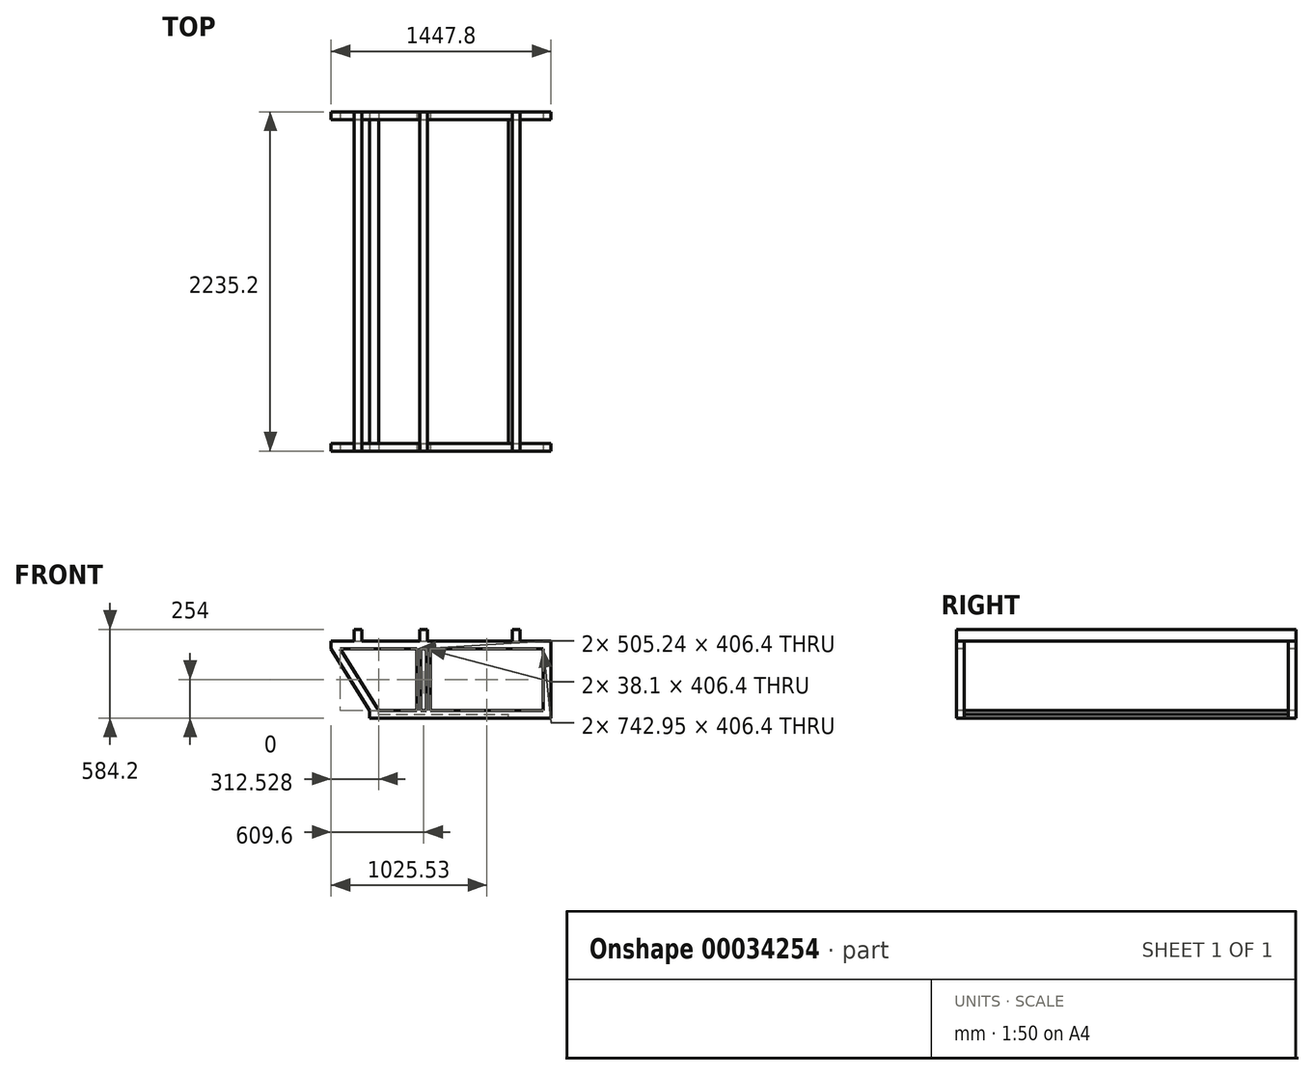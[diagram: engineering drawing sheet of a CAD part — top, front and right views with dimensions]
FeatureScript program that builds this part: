
annotation { "Feature Type Name" : "Feature", "Feature Type Description" : "" }
export const myFeature = defineFeature(function(context is Context, id is Id, definition is map)
    precondition{}
    {
        {
            var Q0;
            Q0=qCreatedBy(makeId("Front.planeOp"),FACE);
            var sketch = newSketch(context, id + "F0", { "sketchPlane" : qUnion([Q0])});
            skLineSegment(sketch, "E0.bottom", {"start": v(0, 0) * mm, "end": v(-1447.8, 0) * mm});
            skLineSegment(sketch, "E0.top", {"start": v(0, -584.2) * mm, "end": v(-1447.8, -584.2) * mm});
            skLineSegment(sketch, "E0.left", {"start": v(0, 0) * mm, "end": v(0, -584.2) * mm});
            skLineSegment(sketch, "E0.right", {"start": v(-1447.8, 0) * mm, "end": v(-1447.8, -584.2) * mm});
            skSolve(sketch);
        }
        {
            var Q0;
            Q0=makeQuery(id+"F0.imprint","IMPRINT",FACE,{"disambiguationData":[TD([[makeQuery(id+"F0.imprint","IMPRINT",EDGE,{"derivedFrom":sQuery(id+"F0.wireOp",EDGE,"E0.bottom")}),1.0]])]});
            extrude(context, id + "F1", {"entities" : qUnion([Q0]), "depth" : 2235.2 * mm});
        }
        {
            var Q0;
            Q0=makeQuery(id+"F1.opExtrude","CAP_FACE",FACE,{"disambiguationData":[OSD([sQuery(id+"F0.wireOp",EDGE,"E0.bottom"),sQuery(id+"F0.wireOp",EDGE,"E0.top"),sQuery(id+"F0.wireOp",EDGE,"E0.left"),sQuery(id+"F0.wireOp",EDGE,"E0.right")])],"isStart":false});
            var sketch = newSketch(context, id + "F2", { "sketchPlane" : qUnion([Q0])});
            skLineSegment(sketch, "E1.bottom", {"start": v(-1447.8, 0) * mm, "end": v(-1295.4, 0) * mm});
            skLineSegment(sketch, "E1.top", {"start": v(-1447.8, -76.2) * mm, "end": v(-1295.4, -76.2) * mm});
            skLineSegment(sketch, "E1.left", {"start": v(-1447.8, 0) * mm, "end": v(-1447.8, -76.2) * mm});
            skLineSegment(sketch, "E1.right", {"start": v(-1295.4, 0) * mm, "end": v(-1295.4, -76.2) * mm});
            skLineSegment(sketch, "E2.bottom", {"start": v(-1244.6, 0) * mm, "end": v(-863.6, 0) * mm});
            skLineSegment(sketch, "E2.top", {"start": v(-1244.6, -76.2) * mm, "end": v(-863.6, -76.2) * mm});
            skLineSegment(sketch, "E2.left", {"start": v(-1244.6, 0) * mm, "end": v(-1244.6, -76.2) * mm});
            skLineSegment(sketch, "E2.right", {"start": v(-863.6, 0) * mm, "end": v(-863.6, -76.2) * mm});
            skLineSegment(sketch, "E3.bottom", {"start": v(-812.8, 0) * mm, "end": v(-254, 0) * mm});
            skLineSegment(sketch, "E3.top", {"start": v(-812.8, -76.2) * mm, "end": v(-254, -76.2) * mm});
            skLineSegment(sketch, "E3.left", {"start": v(-812.8, 0) * mm, "end": v(-812.8, -76.2) * mm});
            skLineSegment(sketch, "E3.right", {"start": v(-254, 0) * mm, "end": v(-254, -76.2) * mm});
            skLineSegment(sketch, "E4.bottom", {"start": v(-203.2, 0) * mm, "end": v(0, 0) * mm});
            skLineSegment(sketch, "E4.top", {"start": v(-203.2, -76.2) * mm, "end": v(0, -76.2) * mm});
            skLineSegment(sketch, "E4.left", {"start": v(-203.2, 0) * mm, "end": v(-203.2, -76.2) * mm});
            skLineSegment(sketch, "E4.right", {"start": v(0, 0) * mm, "end": v(0, -76.2) * mm});
            skSolve(sketch);
        }
        {
            var Q0;
            Q0=makeQuery(id+"F2.imprint","IMPRINT",FACE,{"disambiguationData":[TD([[makeQuery(id+"F2.imprint","IMPRINT",EDGE,{"derivedFrom":sQuery(id+"F2.wireOp",EDGE,"E1.bottom")}),1.0]])]});
            var Q1;
            Q1=makeQuery(id+"F2.imprint","IMPRINT",FACE,{"disambiguationData":[TD([[makeQuery(id+"F2.imprint","IMPRINT",EDGE,{"derivedFrom":sQuery(id+"F2.wireOp",EDGE,"E2.bottom")}),1.0]])]});
            var Q2;
            Q2=makeQuery(id+"F2.imprint","IMPRINT",FACE,{"disambiguationData":[TD([[makeQuery(id+"F2.imprint","IMPRINT",EDGE,{"derivedFrom":sQuery(id+"F2.wireOp",EDGE,"E3.bottom")}),1.0]])]});
            var Q3;
            Q3=makeQuery(id+"F2.imprint","IMPRINT",FACE,{"disambiguationData":[TD([[makeQuery(id+"F2.imprint","IMPRINT",EDGE,{"derivedFrom":sQuery(id+"F2.wireOp",EDGE,"E4.bottom")}),1.0]])]});
            extrude(context, id + "F3", {"entities" : qUnion([Q0, Q1, Q2, Q3]), "operationType" : NewBodyOperationType.REMOVE, "endBound" : BoundingType.THROUGH_ALL, "oppositeDirection" : true, "depth" : 25.4 * mm});
        }
        {
            var Q0;
            Q0=makeQuery(id+"F1.opExtrude","CAP_FACE",FACE,{"disambiguationData":[OSD([sQuery(id+"F0.wireOp",EDGE,"E0.bottom"),sQuery(id+"F0.wireOp",EDGE,"E0.top"),sQuery(id+"F0.wireOp",EDGE,"E0.left"),sQuery(id+"F0.wireOp",EDGE,"E0.right")])],"isStart":false});
            var sketch = newSketch(context, id + "F4", { "sketchPlane" : qUnion([Q0])});
            skLineSegment(sketch, "E5.right", {"start": v(-1193.8, -584.2) * mm, "end": v(-1193.8, -533.4) * mm});
            skLineSegment(sketch, "E6", {"start": v(-1447.8, -127) * mm, "end": v(-1193.8, -533.4) * mm});
            skLineSegment(sketch, "E7", {"start": v(-1447.8, -127) * mm, "end": v(-1447.8, -584.2) * mm});
            skLineSegment(sketch, "E8", {"start": v(-1447.8, -584.2) * mm, "end": v(-1193.8, -584.2) * mm});
            skLineSegment(sketch, "E9.top", {"start": v(-1387.9, -127) * mm, "end": v(-819.15, -127) * mm});
            skLineSegment(sketch, "E10", {"start": v(-1387.9, -127) * mm, "end": v(-1133.9, -533.4) * mm});
            skPoint(sketch, "E11.startSnap0", {"position": v(-838.2, 0) * mm});
            skLineSegment(sketch, "E12.bottom", {"start": v(-857.25, -127) * mm, "end": v(-882.65, -127) * mm});
            skLineSegment(sketch, "E12.top", {"start": v(-857.25, -533.4) * mm, "end": v(-882.65, -533.4) * mm});
            skLineSegment(sketch, "E12.left", {"start": v(-857.25, -127) * mm, "end": v(-857.25, -533.4) * mm});
            skLineSegment(sketch, "E12.right", {"start": v(-882.65, -127) * mm, "end": v(-882.65, -533.4) * mm});
            skLineSegment(sketch, "E13.left", {"start": v(-819.15, -127) * mm, "end": v(-819.15, -533.4) * mm});
            skPoint(sketch, "E11.start.orphan", {"position": v(-838.2, -127) * mm});
            skLineSegment(sketch, "E14.trimOffspring", {"start": v(-819.15, -533.4) * mm, "end": v(-1133.9, -533.4) * mm});
            skPoint(sketch, "E9.right.end.orphan", {"position": v(0, -127) * mm});
            skSolve(sketch);
        }
        {
            var Q0;
            Q0=makeQuery(id+"F4.imprint","IMPRINT",FACE,{"disambiguationData":[TD([[makeQuery(id+"F4.imprint","IMPRINT",EDGE,{"derivedFrom":sQuery(id+"F4.wireOp",EDGE,"E5.right")}),1.0]])]});
            var Q1;
            {var subQ1=sQuery(id+"F4.wireOp",EDGE,"E10");Q1=makeQuery(id+"F4.imprint","IMPRINT",FACE,{"disambiguationData":[TD([[makeQuery(id+"F4.imprint","IMPRINT",EDGE,{"derivedFrom":subQ1}),1.0]])]});}
            var Q2;
            {var subQ1=sQuery(id+"F4.wireOp",EDGE,"E12.left");Q2=makeQuery(id+"F4.imprint","IMPRINT",FACE,{"disambiguationData":[TD([[makeQuery(id+"F4.imprint","IMPRINT",EDGE,{"derivedFrom":subQ1}),1.0]])]});}
            extrude(context, id + "F5", {"entities" : qUnion([Q0, Q1, Q2]), "operationType" : NewBodyOperationType.REMOVE, "endBound" : BoundingType.THROUGH_ALL, "oppositeDirection" : true, "depth" : 25.4 * mm});
        }
        {
            var Q0;
            Q0=makeQuery(id+"F1.opExtrude","CAP_FACE",FACE,{"disambiguationData":[OSD([sQuery(id+"F0.wireOp",EDGE,"E0.bottom"),sQuery(id+"F0.wireOp",EDGE,"E0.top"),sQuery(id+"F0.wireOp",EDGE,"E0.left"),sQuery(id+"F0.wireOp",EDGE,"E0.right")])],"isStart":false});
            var sketch = newSketch(context, id + "F6", { "sketchPlane" : qUnion([Q0])});
            skLineSegment(sketch, "E15.bottom", {"start": v(-793.75, -127) * mm, "end": v(-50.8, -127) * mm});
            skLineSegment(sketch, "E15.top", {"start": v(-793.75, -533.4) * mm, "end": v(-50.8, -533.4) * mm});
            skLineSegment(sketch, "E15.left", {"start": v(-793.75, -127) * mm, "end": v(-793.75, -533.4) * mm});
            skLineSegment(sketch, "E15.right", {"start": v(-50.8, -127) * mm, "end": v(-50.8, -533.4) * mm});
            skSolve(sketch);
        }
        {
            var Q0;
            Q0=makeQuery(id+"F6.imprint","IMPRINT",FACE,{"disambiguationData":[TD([[makeQuery(id+"F6.imprint","IMPRINT",EDGE,{"derivedFrom":sQuery(id+"F6.wireOp",EDGE,"E15.bottom")}),-1.0]])]});
            extrude(context, id + "F7", {"entities" : qUnion([Q0]), "operationType" : NewBodyOperationType.REMOVE, "endBound" : BoundingType.THROUGH_ALL, "oppositeDirection" : true, "depth" : 25.4 * mm});
        }
        {
            var Q0;
            Q0=makeQuery(id+"F1.opExtrude","SWEPT_FACE",FACE,{"disambiguationData":[OSD([sQuery(id+"F0.wireOp",EDGE,"E0.left")])]});
            var sketch = newSketch(context, id + "F8", { "sketchPlane" : qUnion([Q0])});
            skLineSegment(sketch, "E16.bottom", {"start": v(-2184.4, -76.2) * mm, "end": v(-50.8, -76.2) * mm});
            skLineSegment(sketch, "E16.top", {"start": v(-2184.4, -533.4) * mm, "end": v(-50.8, -533.4) * mm});
            skLineSegment(sketch, "E16.left", {"start": v(-2184.4, -76.2) * mm, "end": v(-2184.4, -533.4) * mm});
            skLineSegment(sketch, "E16.right", {"start": v(-50.8, -76.2) * mm, "end": v(-50.8, -533.4) * mm});
            skSolve(sketch);
        }
        {
            var Q0;
            Q0=makeQuery(id+"F8.imprint","IMPRINT",FACE,{"disambiguationData":[TD([[makeQuery(id+"F8.imprint","IMPRINT",EDGE,{"derivedFrom":sQuery(id+"F8.wireOp",EDGE,"E16.bottom")}),-1.0]])]});
            var Q1;
            Q1=makeQuery(id+"F8.imprint","IMPRINT",FACE,{"disambiguationData":[TD([[makeQuery(id+"F8.imprint","IMPRINT",EDGE,{"derivedFrom":sQuery(id+"F8.wireOp",EDGE,"E16.bottom")}),1.0]])]});
            extrude(context, id + "F9", {"entities" : qUnion([Q0, Q1]), "operationType" : NewBodyOperationType.REMOVE, "endBound" : BoundingType.THROUGH_ALL, "oppositeDirection" : true, "depth" : 25.4 * mm});
        }
        {
            var Q0;
            Q0=qCreatedBy(makeId("Top.planeOp"),FACE);
            var sketch = newSketch(context, id + "F10", { "sketchPlane" : qUnion([Q0])});
            skLineSegment(sketch, "E17.bottom", {"start": v(-1244.6, -50.8) * mm, "end": v(-863.6, -50.8) * mm});
            skLineSegment(sketch, "E17.top", {"start": v(-1244.6, -2184.4) * mm, "end": v(-863.6, -2184.4) * mm});
            skLineSegment(sketch, "E17.left", {"start": v(-1244.6, -50.8) * mm, "end": v(-1244.6, -2184.4) * mm});
            skLineSegment(sketch, "E17.right", {"start": v(-863.6, -50.8) * mm, "end": v(-863.6, -2184.4) * mm});
            skLineSegment(sketch, "E18.bottom", {"start": v(-812.8, -50.8) * mm, "end": v(-254, -50.8) * mm});
            skLineSegment(sketch, "E18.top", {"start": v(-812.8, -2184.4) * mm, "end": v(-254, -2184.4) * mm});
            skLineSegment(sketch, "E18.left", {"start": v(-812.8, -50.8) * mm, "end": v(-812.8, -2184.4) * mm});
            skLineSegment(sketch, "E18.right", {"start": v(-254, -50.8) * mm, "end": v(-254, -2184.4) * mm});
            skLineSegment(sketch, "E19.bottom", {"start": v(0, -50.8) * mm, "end": v(-203.2, -50.8) * mm});
            skLineSegment(sketch, "E19.top", {"start": v(0, -2184.4) * mm, "end": v(-203.2, -2184.4) * mm});
            skLineSegment(sketch, "E19.left", {"start": v(0, -50.8) * mm, "end": v(0, -2184.4) * mm});
            skLineSegment(sketch, "E19.right", {"start": v(-203.2, -50.8) * mm, "end": v(-203.2, -2184.4) * mm});
            skLineSegment(sketch, "E20.bottom", {"start": v(-1447.8, -50.8) * mm, "end": v(-1295.4, -50.8) * mm});
            skLineSegment(sketch, "E20.top", {"start": v(-1447.8, -2184.4) * mm, "end": v(-1295.4, -2184.4) * mm});
            skLineSegment(sketch, "E20.left", {"start": v(-1447.8, -50.8) * mm, "end": v(-1447.8, -2184.4) * mm});
            skLineSegment(sketch, "E20.right", {"start": v(-1295.4, -50.8) * mm, "end": v(-1295.4, -2184.4) * mm});
            skSolve(sketch);
        }
        {
            var Q0;
            Q0=makeQuery(id+"F10.imprint","IMPRINT",FACE,{"disambiguationData":[TD([[makeQuery(id+"F10.imprint","IMPRINT",EDGE,{"derivedFrom":sQuery(id+"F10.wireOp",EDGE,"E20.bottom")}),-1.0]])]});
            var Q1;
            Q1=makeQuery(id+"F10.imprint","IMPRINT",FACE,{"disambiguationData":[TD([[makeQuery(id+"F10.imprint","IMPRINT",EDGE,{"derivedFrom":sQuery(id+"F10.wireOp",EDGE,"E17.bottom")}),-1.0]])]});
            var Q2;
            Q2=makeQuery(id+"F10.imprint","IMPRINT",FACE,{"disambiguationData":[TD([[makeQuery(id+"F10.imprint","IMPRINT",EDGE,{"derivedFrom":sQuery(id+"F10.wireOp",EDGE,"E18.bottom")}),-1.0]])]});
            var Q3;
            Q3=makeQuery(id+"F10.imprint","IMPRINT",FACE,{"disambiguationData":[TD([[makeQuery(id+"F10.imprint","IMPRINT",EDGE,{"derivedFrom":sQuery(id+"F10.wireOp",EDGE,"E19.bottom")}),1.0]])]});
            extrude(context, id + "F11", {"entities" : qUnion([Q0, Q1, Q2, Q3]), "operationType" : NewBodyOperationType.REMOVE, "oppositeDirection" : true, "depth" : 127 * mm});
        }
        {
            var Q0;
            {var subQ0=sQuery(id+"F4.wireOp",EDGE,"E14.trimOffspring");Q0=makeQuery(id+"F9.boolean.opBoolean","MERGE",FACE,{"derivedFrom":[makeQuery(id+"F5.boolean.opBoolean","COPY",FACE,{"derivedFrom":makeQuery(id+"F5.opExtrude","SWEPT_FACE",FACE,{"disambiguationData":[OSD([subQ0]),TDD([makeQuery(id+"F4.imprint","IMPRINT",EDGE,{"disambiguationData":[TD([[makeQuery(id+"F4.imprint","INTERSECT",VERTEX,{"derivedFrom":[sQuery(id+"F4.wireOp",EDGE,"E12.left"),subQ0]}),1.0]])],"derivedFrom":subQ0})])]})}),makeQuery(id+"F5.boolean.opBoolean","COPY",FACE,{"derivedFrom":makeQuery(id+"F5.opExtrude","SWEPT_FACE",FACE,{"disambiguationData":[OSD([subQ0]),TDD([makeQuery(id+"F4.imprint","IMPRINT",EDGE,{"disambiguationData":[TD([[makeQuery(id+"F4.imprint","INTERSECT",VERTEX,{"derivedFrom":[sQuery(id+"F4.wireOp",EDGE,"E10"),subQ0]}),1.0]])],"derivedFrom":subQ0})])]})}),makeQuery(id+"F7.boolean.opBoolean","COPY",FACE,{"derivedFrom":makeQuery(id+"F7.opExtrude","SWEPT_FACE",FACE,{"disambiguationData":[OSD([sQuery(id+"F6.wireOp",EDGE,"E15.top")])]})}),makeQuery(id+"F9.opExtrude","SWEPT_FACE",FACE,{"disambiguationData":[OSD([sQuery(id+"F8.wireOp",EDGE,"E16.top")])]})]});}
            var sketch = newSketch(context, id + "F12", { "sketchPlane" : qUnion([Q0])});
            skLineSegment(sketch, "E21.bottom", {"start": v(-1133.9, -50.8) * mm, "end": v(-50.8, -50.8) * mm});
            skLineSegment(sketch, "E21.top", {"start": v(-1133.9, -2184.4) * mm, "end": v(-50.8, -2184.4) * mm});
            skLineSegment(sketch, "E21.left", {"start": v(-1133.9, -50.8) * mm, "end": v(-1133.9, -2184.4) * mm});
            skLineSegment(sketch, "E21.right", {"start": v(-50.8, -50.8) * mm, "end": v(-50.8, -2184.4) * mm});
            skSolve(sketch);
        }
        {
            var Q0;
            {var subQ1=sQuery(id+"F12.wireOp",EDGE,"E21.left");Q0=makeQuery(id+"F12.imprint","IMPRINT",FACE,{"disambiguationData":[TD([[makeQuery(id+"F12.imprint","IMPRINT",EDGE,{"derivedFrom":subQ1}),1.0]])]});}
            extrude(context, id + "F13", {"entities" : qUnion([Q0]), "operationType" : NewBodyOperationType.REMOVE, "oppositeDirection" : true, "depth" : 25.4 * mm});
        }
        {
            var Q0;
            {var subQ0=sQuery(id+"F4.wireOp",EDGE,"E14.trimOffspring");var subQ1=makeQuery(id+"F5.boolean.opBoolean","COPY",FACE,{"derivedFrom":makeQuery(id+"F5.opExtrude","SWEPT_FACE",FACE,{"disambiguationData":[OSD([subQ0]),TDD([makeQuery(id+"F4.imprint","IMPRINT",EDGE,{"disambiguationData":[TD([[makeQuery(id+"F4.imprint","INTERSECT",VERTEX,{"derivedFrom":[sQuery(id+"F4.wireOp",EDGE,"E12.left"),subQ0]}),1.0]])],"derivedFrom":subQ0})])]})});var subQ2=makeQuery(id+"F5.boolean.opBoolean","COPY",FACE,{"derivedFrom":makeQuery(id+"F5.opExtrude","SWEPT_FACE",FACE,{"disambiguationData":[OSD([subQ0]),TDD([makeQuery(id+"F4.imprint","IMPRINT",EDGE,{"disambiguationData":[TD([[makeQuery(id+"F4.imprint","INTERSECT",VERTEX,{"derivedFrom":[sQuery(id+"F4.wireOp",EDGE,"E10"),subQ0]}),1.0]])],"derivedFrom":subQ0})])]})});var subQ3=makeQuery(id+"F7.boolean.opBoolean","COPY",FACE,{"derivedFrom":makeQuery(id+"F7.opExtrude","SWEPT_FACE",FACE,{"disambiguationData":[OSD([sQuery(id+"F6.wireOp",EDGE,"E15.top")])]})});var subQ4=makeQuery(id+"F9.opExtrude","SWEPT_FACE",FACE,{"disambiguationData":[OSD([sQuery(id+"F8.wireOp",EDGE,"E16.top")])]});Q0=makeQuery(id+"F13.boolean.opBoolean","SPLIT",FACE,{"disambiguationData":[TD([makeQuery(id+"F1.opExtrude","SWEPT_FACE",FACE,{"disambiguationData":[OSD([sQuery(id+"F0.wireOp",EDGE,"E0.left")])]}),subQ1,subQ2,subQ3,makeQuery(id+"F7.boolean.opBoolean","COPY",FACE,{"derivedFrom":makeQuery(id+"F7.opExtrude","SWEPT_FACE",FACE,{"disambiguationData":[OSD([sQuery(id+"F6.wireOp",EDGE,"E15.right")])]})}),subQ4,makeQuery(id+"F9.boolean.opBoolean","COPY",FACE,{"derivedFrom":makeQuery(id+"F9.opExtrude","SWEPT_FACE",FACE,{"disambiguationData":[OSD([sQuery(id+"F8.wireOp",EDGE,"E16.left")])]})}),makeQuery(id+"F9.boolean.opBoolean","COPY",FACE,{"derivedFrom":makeQuery(id+"F9.opExtrude","SWEPT_FACE",FACE,{"disambiguationData":[OSD([sQuery(id+"F8.wireOp",EDGE,"E16.right")])]})}),makeQuery(id+"F13.opExtrude","SWEPT_FACE",FACE,{"disambiguationData":[OSD([sQuery(id+"F12.wireOp",EDGE,"E21.bottom")])]}),makeQuery(id+"F13.opExtrude","SWEPT_FACE",FACE,{"disambiguationData":[OSD([sQuery(id+"F12.wireOp",EDGE,"E21.top")])]}),makeQuery(id+"F13.opExtrude","SWEPT_FACE",FACE,{"disambiguationData":[OSD([sQuery(id+"F12.wireOp",EDGE,"E21.right")])]})])],"derivedFrom":makeQuery(id+"F9.boolean.opBoolean","MERGE",FACE,{"derivedFrom":[subQ1,subQ2,subQ3,subQ4]})});}
            var sketch = newSketch(context, id + "F14", { "sketchPlane" : qUnion([Q0])});
            skLineSegment(sketch, "E22.bottom", {"start": v(0, -50.8) * mm, "end": v(-279.4, -50.8) * mm});
            skLineSegment(sketch, "E22.top", {"start": v(0, -2184.4) * mm, "end": v(-279.4, -2184.4) * mm});
            skLineSegment(sketch, "E22.left", {"start": v(0, -50.8) * mm, "end": v(0, -2184.4) * mm});
            skLineSegment(sketch, "E22.right", {"start": v(-279.4, -50.8) * mm, "end": v(-279.4, -2184.4) * mm});
            skSolve(sketch);
        }
        {
            var Q0;
            {var subQ1=sQuery(id+"F14.wireOp",EDGE,"E22.right");Q0=makeQuery(id+"F14.imprint","IMPRINT",FACE,{"disambiguationData":[TD([[makeQuery(id+"F14.imprint","IMPRINT",EDGE,{"derivedFrom":subQ1}),1.0]])]});}
            var Q1;
            {var subQ1=sQuery(id+"F14.wireOp",EDGE,"E22.left");Q1=makeQuery(id+"F14.imprint","IMPRINT",FACE,{"disambiguationData":[TD([[makeQuery(id+"F14.imprint","IMPRINT",EDGE,{"derivedFrom":subQ1}),1.0]])]});}
            extrude(context, id + "F15", {"entities" : qUnion([Q0, Q1]), "operationType" : NewBodyOperationType.REMOVE, "endBound" : BoundingType.THROUGH_ALL, "oppositeDirection" : true, "depth" : 25.4 * mm});
        }
    });
